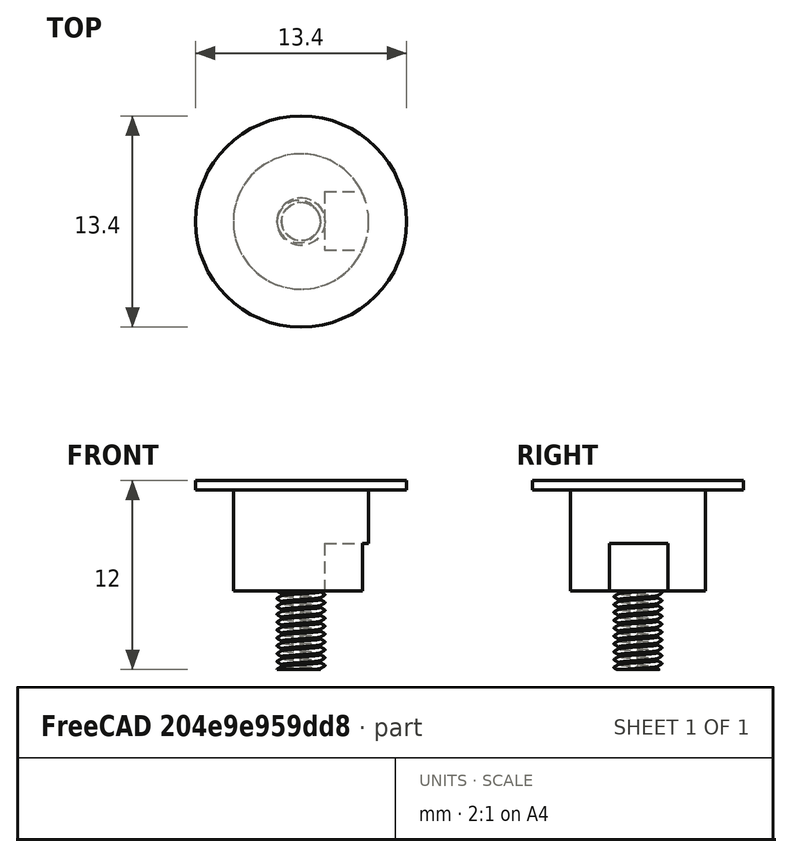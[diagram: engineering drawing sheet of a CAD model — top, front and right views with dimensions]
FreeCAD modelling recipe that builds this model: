
FCSTD DOCUMENT  (FreeCAD 0.20R29603 (Git))
Label: gearscrew
License: All rights reserved
LicenseURL: http://en.wikipedia.org/wiki/All_rights_reserved
objects: PartDesign::AdditiveCylinder×2, PartDesign::SubtractiveBox×1, PartDesign::Body×1, Part::FeaturePython×1
note: 8 computed .brp shape members not serialized (recipe doc carries the construction recipe); baked Part::Feature solids carry a one-line shape summary decoded from their .brp

FEATURE [PartDesign::AdditiveCylinder] Cylinder
  Angle = 360
  AttacherType = Attacher::AttachEngine3D
  FirstAngle = 0
  Height = 6.4
  MapMode = 5
  Radius = 4.3
  SecondAngle = 0
  Support = -> [XY_Plane]
FEATURE [PartDesign::AdditiveCylinder] Cylinder001
  Angle = 360
  AttacherType = Attacher::AttachEngine3D
  BaseFeature = -> Cylinder
  FirstAngle = 0
  Height = 0.6
  MapMode = 5
  Placement = pos=(0,0,6.4) rot=(0,0,1;0rad)
  Radius = 6.7
  SecondAngle = 0
  Support = -> [Cylinder]
FEATURE [PartDesign::SubtractiveBox] Box
  AttacherType = Attacher::AttachEngine3D
  AttachmentOffset = pos=(1.5,-1.9,3.4) rot=(0,0,1;0rad)
  BaseFeature = -> Cylinder001
  Height = 13
  Length = 3
  MapMode = 5
  Placement = pos=(1.5,1.9,3) rot=(1,0,0;3.14159rad)
  Support = -> [Cylinder001]
  Width = 3.7
FEATURE [PartDesign::Body] Body
  Group = -> [Cylinder,Cylinder001,Box]
  Origin = -> Origin
  Tip = -> Box
FEATURE [Part::FeaturePython] ScrewTap  label="M3x5-ScrewTap"  # Fasteners workbench fastener (typed FeaturePython)
  diameter = 4
  diameterCustom = 3
  invert = false
  leftHanded = false
  length = 5
  matchOuter = false
  offset = 0
  pitchCustom = 1
  thread = true
  type = 2
